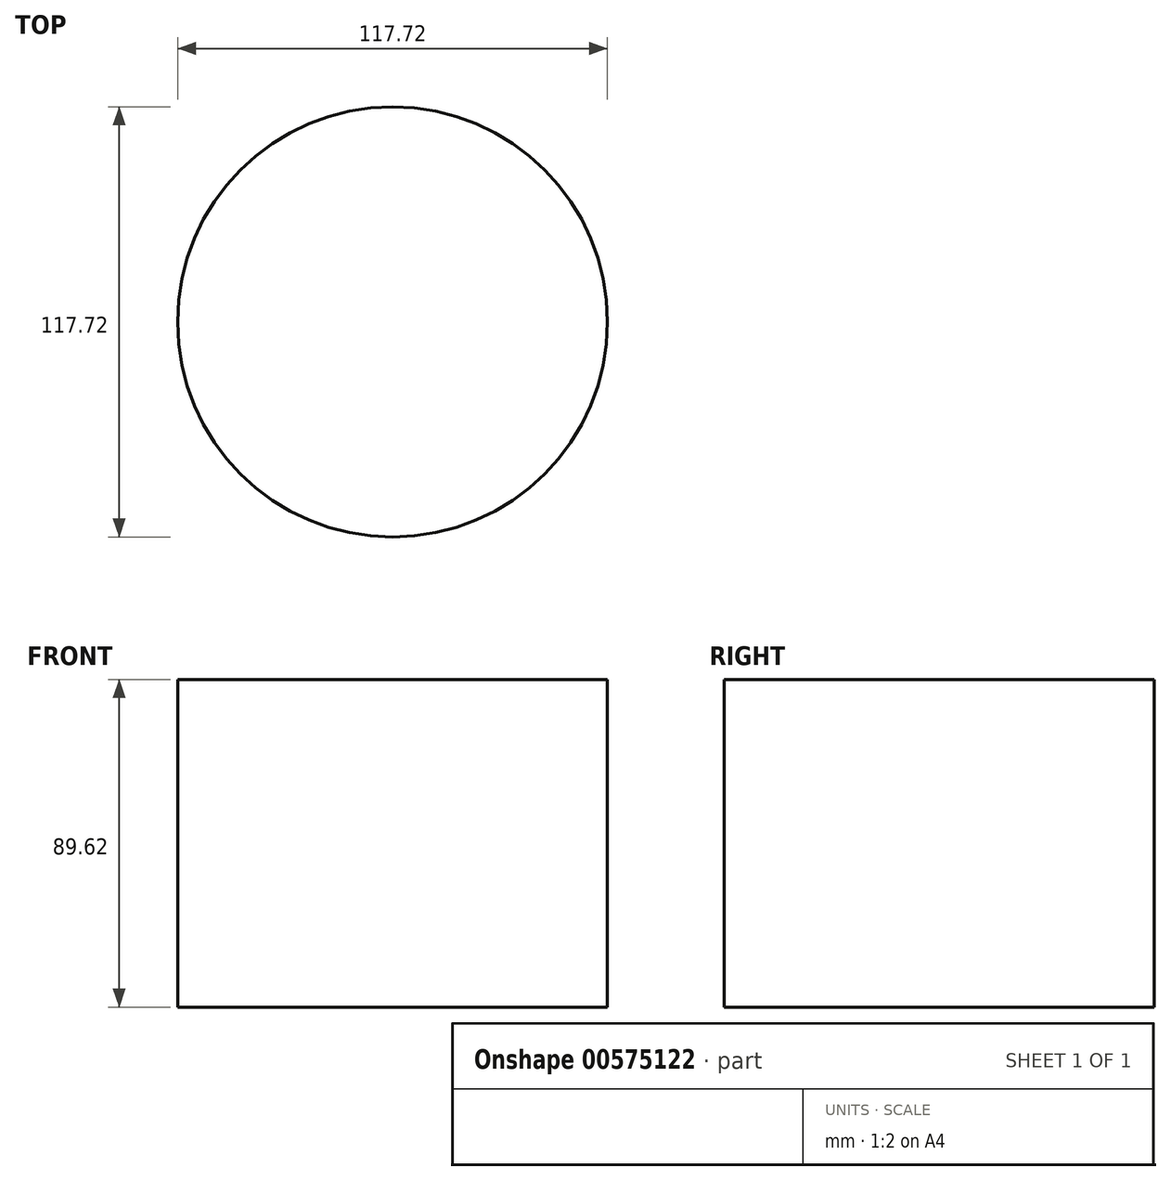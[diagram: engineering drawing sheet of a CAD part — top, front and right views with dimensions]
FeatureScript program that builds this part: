
annotation { "Feature Type Name" : "Feature", "Feature Type Description" : "" }
export const myFeature = defineFeature(function(context is Context, id is Id, definition is map)
    precondition{}
    {
        {
            var Q0;
            Q0=qCreatedBy(makeId("Top.planeOp"),FACE);
            var sketch = newSketch(context, id + "F0", { "sketchPlane" : qUnion([Q0])});
            skCircle(sketch, "E0", {"center": v(0, 0) * mm, "radius": 58.86 * mm});
            skSolve(sketch);
        }
        {
            var Q0;
            Q0=makeQuery(id+"F0.imprint","IMPRINT",FACE,{"disambiguationData":[TD([[makeQuery(id+"F0.imprint","IMPRINT",EDGE,{"derivedFrom":sQuery(id+"F0.wireOp",EDGE,"E0")}),1.0]])]});
            extrude(context, id + "F1", {"entities" : qUnion([Q0]), "endBound" : BoundingType.SYMMETRIC, "depth" : 0.1 * yard, "offsetDistance" : 0.03 * yard});
        }
    });
